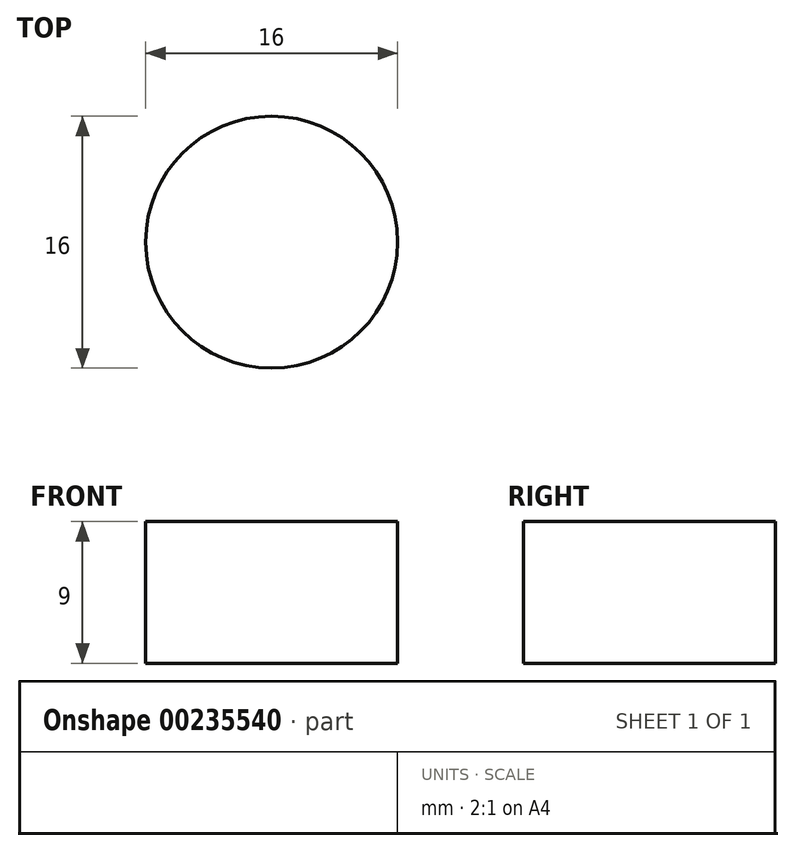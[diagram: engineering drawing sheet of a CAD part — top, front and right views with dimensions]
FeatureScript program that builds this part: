
annotation { "Feature Type Name" : "Feature", "Feature Type Description" : "" }
export const myFeature = defineFeature(function(context is Context, id is Id, definition is map)
    precondition{}
    {
        {
            var Q0;
            Q0=qCreatedBy(makeId("Top.planeOp"),FACE);
            var sketch = newSketch(context, id + "F0", { "sketchPlane" : qUnion([Q0])});
            skCircle(sketch, "E0", {"center": v(0, 0) * mm, "radius": 8 * mm});
            skSolve(sketch);
        }
        {
            var Q0;
            Q0 = qSketchRegion(id + "F0", true);
            extrude(context, id + "F1", {"entities" : qUnion([Q0]), "depth" : 9 * mm});
        }
    });
